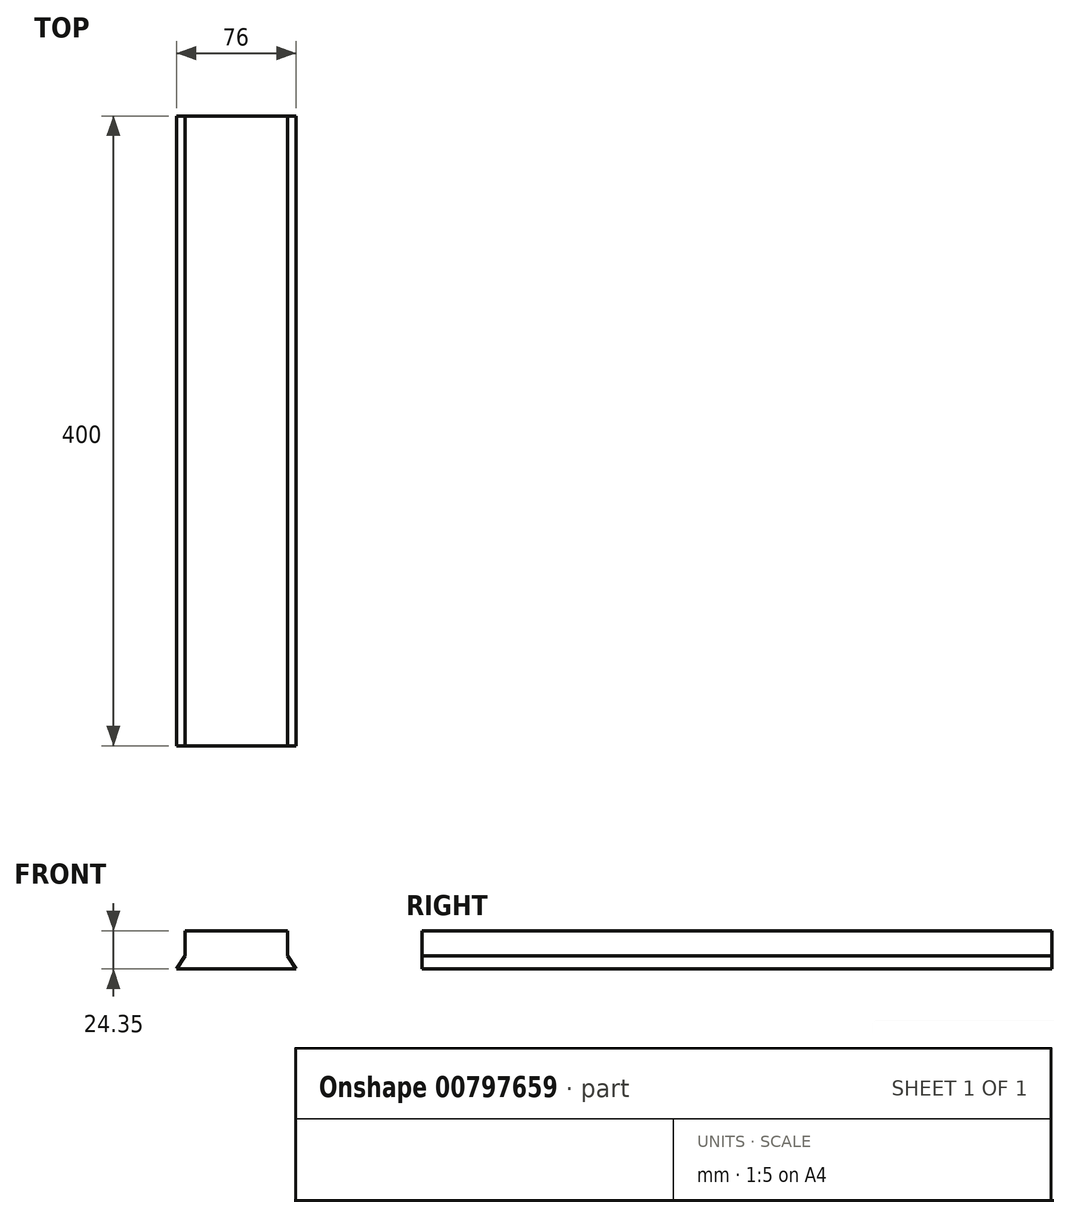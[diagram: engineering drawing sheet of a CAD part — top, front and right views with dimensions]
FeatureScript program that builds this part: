
annotation { "Feature Type Name" : "Feature", "Feature Type Description" : "" }
export const myFeature = defineFeature(function(context is Context, id is Id, definition is map)
    precondition{}
    {
        {
            var Q0;
            Q0=qCreatedBy(makeId("Front.planeOp"),FACE);
            var sketch = newSketch(context, id + "F0", { "sketchPlane" : qUnion([Q0])});
            skLineSegment(sketch, "E0", {"start": v(-49.36, -4.27) * mm, "end": v(26.64, -4.27) * mm});
            skLineSegment(sketch, "E1", {"start": v(26.64, -4.27) * mm, "end": v(21.14, 4.08) * mm});
            skLineSegment(sketch, "E2", {"start": v(-43.86, 4.08) * mm, "end": v(-49.36, -4.27) * mm});
            skLineSegment(sketch, "E3", {"start": v(-43.86, 4.08) * mm, "end": v(21.14, 4.08) * mm});
            skSolve(sketch);
        }
        {
            var Q0;
            Q0=makeQuery(id+"F0.imprint","IMPRINT",FACE,{"disambiguationData":[TD([[makeQuery(id+"F0.imprint","IMPRINT",EDGE,{"derivedFrom":sQuery(id+"F0.wireOp",EDGE,"E0")}),1.0]])]});
            extrude(context, id + "F1", {"entities" : qUnion([Q0]), "depth" : 400 * mm, "offsetDistance" : 25 * mm});
        }
        {
            var Q0;
            Q0=qCreatedBy(makeId("Front.planeOp"),FACE);
            var sketch = newSketch(context, id + "F2", { "sketchPlane" : qUnion([Q0])});
            skLineSegment(sketch, "E4", {"start": v(-43.86, 4.08) * mm, "end": v(-43.86, 20.08) * mm});
            skLineSegment(sketch, "E5", {"start": v(-43.86, 20.08) * mm, "end": v(21.14, 20.08) * mm});
            skLineSegment(sketch, "E6", {"start": v(21.14, 20.08) * mm, "end": v(21.14, 4.08) * mm});
            skLineSegment(sketch, "E7", {"start": v(21.14, 4.08) * mm, "end": v(-43.86, 4.08) * mm});
            skSolve(sketch);
        }
        {
            var Q0;
            Q0 = qSketchRegion(id + "F2", true);
            extrude(context, id + "F3", {"entities" : qUnion([Q0]), "operationType" : NewBodyOperationType.ADD, "depth" : 400 * mm, "offsetDistance" : 25 * mm});
        }
    });
